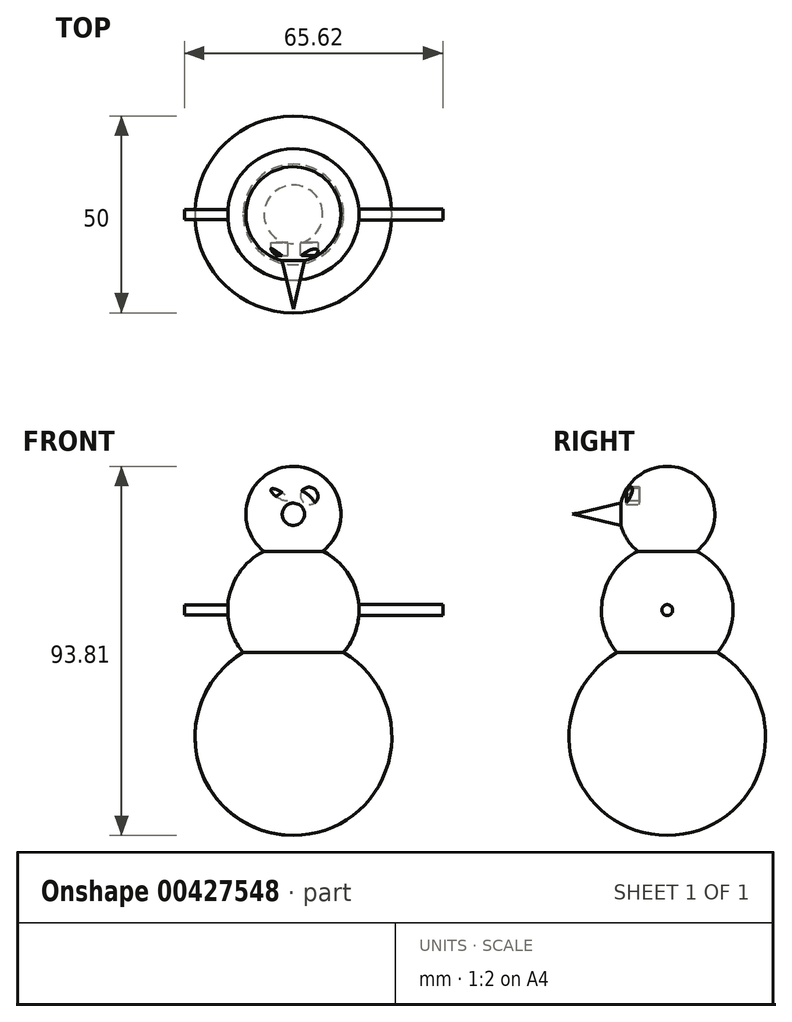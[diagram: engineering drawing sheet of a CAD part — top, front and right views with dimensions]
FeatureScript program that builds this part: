
annotation { "Feature Type Name" : "Feature", "Feature Type Description" : "" }
export const myFeature = defineFeature(function(context is Context, id is Id, definition is map)
    precondition{}
    {
        {
            var Q0;
            Q0=qCreatedBy(makeId("Front.planeOp"),FACE);
            var sketch = newSketch(context, id + "F0", { "sketchPlane" : qUnion([Q0])});
            skArc(sketch, "E0", {"start": v(-7.46, 14.94) * mm, "mid": v(-16.36, 3.37) * mm, "end": v(-12.77, -10.77) * mm});
            skArc(sketch, "E1", {"start": v(0, 36.54) * mm, "mid": v(-11.43, 28.4) * mm, "end": v(-7.46, 14.94) * mm});
            skArc(sketch, "E2", {"start": v(-12.77, -10.77) * mm, "mid": v(-24.1, -38.88) * mm, "end": v(0, -57.27) * mm});
            skLineSegment(sketch, "E3", {"start": v(0, 36.54) * mm, "end": v(0, -57.27) * mm});
            skSolve(sketch);
        }
        {
            var Q0;
            Q0 = qSketchRegion(id + "F0", true);
            var Q1;
            Q1=sQuery(id+"F0.wireOp",EDGE,"E3");
            revolve(context, id + "F1", {"entities" : qUnion([Q0]), "axis" : qUnion([Q1]), "revolveType" : RevolveType.FULL});
        }
        {
            var Q0;
            Q0=qCreatedBy(makeId("Right.planeOp"),FACE);
            var sketch = newSketch(context, id + "F2", { "sketchPlane" : qUnion([Q0])});
            skLineSegment(sketch, "E4", {"start": v(-11.49, 24.36) * mm, "end": v(-24.02, 24.36) * mm});
            skLineSegment(sketch, "E5", {"start": v(-24.02, 24.36) * mm, "end": v(-11.37, 27.28) * mm});
            skLineSegment(sketch, "E6", {"start": v(-11.37, 27.28) * mm, "end": v(-11.49, 24.36) * mm});
            skSolve(sketch);
        }
        {
            var Q0;
            Q0 = qSketchRegion(id + "F2", true);
            var Q1;
            Q1=sQuery(id+"F2.wireOp",EDGE,"E4");
            revolve(context, id + "F3", {"operationType" : NewBodyOperationType.ADD, "entities" : qUnion([Q0]), "axis" : qUnion([Q1]), "revolveType" : RevolveType.FULL});
        }
        {
            var Q0;
            Q0=qCreatedBy(makeId("Front.planeOp"),FACE);
            cPlane(context, id + "F4", {"entities" : qUnion([Q0]), "cplaneType" : CPlaneType.OFFSET, "offset" : 10.4 * mm, "width" : 152.4 * mm, "height" : 152.4 * mm});
        }
        {
            var Q0;
            Q0=qCreatedBy(id+"F4.planeOp",FACE);
            var sketch = newSketch(context, id + "F5", { "sketchPlane" : qUnion([Q0])});
            skEllipse(sketch, "E7", {"center": v(-3.56, 29.34) * mm, "majorRadius": 2.51 * mm, "minorRadius": 0.83 * mm, "majorAxis": v(-0.85, 0.53)});
            skEllipse(sketch, "E8", {"center": v(4.04, 29.03) * mm, "majorRadius": 2.18 * mm, "minorRadius": 2.24 * mm, "majorAxis": v(0.59, 0.8)});
            skSolve(sketch);
        }
        {
            var Q0;
            Q0 = qSketchRegion(id + "F5", true);
            extrude(context, id + "F6", {"entities" : qUnion([Q0]), "operationType" : NewBodyOperationType.REMOVE, "oppositeDirection" : true, "depth" : 3.3 * mm});
        }
        {
            var Q0;
            Q0=qCreatedBy(makeId("Front.planeOp"),FACE);
            var sketch = newSketch(context, id + "F7", { "sketchPlane" : qUnion([Q0])});
            skLineSegment(sketch, "E9", {"start": v(0, 0) * mm, "end": v(-27.64, 0) * mm});
            skLineSegment(sketch, "E10", {"start": v(-27.64, 0) * mm, "end": v(-27.64, 1.26) * mm});
            skLineSegment(sketch, "E11", {"start": v(-27.64, 1.26) * mm, "end": v(-13.82, 1.26) * mm});
            skPoint(sketch, "E11.endSnap0", {"position": v(-13.82, 0) * mm});
            skLineSegment(sketch, "E12", {"start": v(-13.82, 1.26) * mm, "end": v(-13.82, 0) * mm});
            skLineSegment(sketch, "E13", {"start": v(0, 0) * mm, "end": v(37.98, 0) * mm});
            skLineSegment(sketch, "E14", {"start": v(37.98, 0) * mm, "end": v(37.98, 1.38) * mm});
            skLineSegment(sketch, "E15", {"start": v(37.98, 1.38) * mm, "end": v(0, 1.38) * mm});
            skLineSegment(sketch, "E16", {"start": v(0, 1.38) * mm, "end": v(0, 0) * mm});
            skSolve(sketch);
        }
        {
            var Q0;
            Q0 = qSketchRegion(id + "F7", true);
            var Q1;
            Q1=sQuery(id+"F7.wireOp",EDGE,"E9");
            revolve(context, id + "F8", {"operationType" : NewBodyOperationType.ADD, "entities" : qUnion([Q0]), "axis" : qUnion([Q1]), "revolveType" : RevolveType.FULL});
        }
    });
